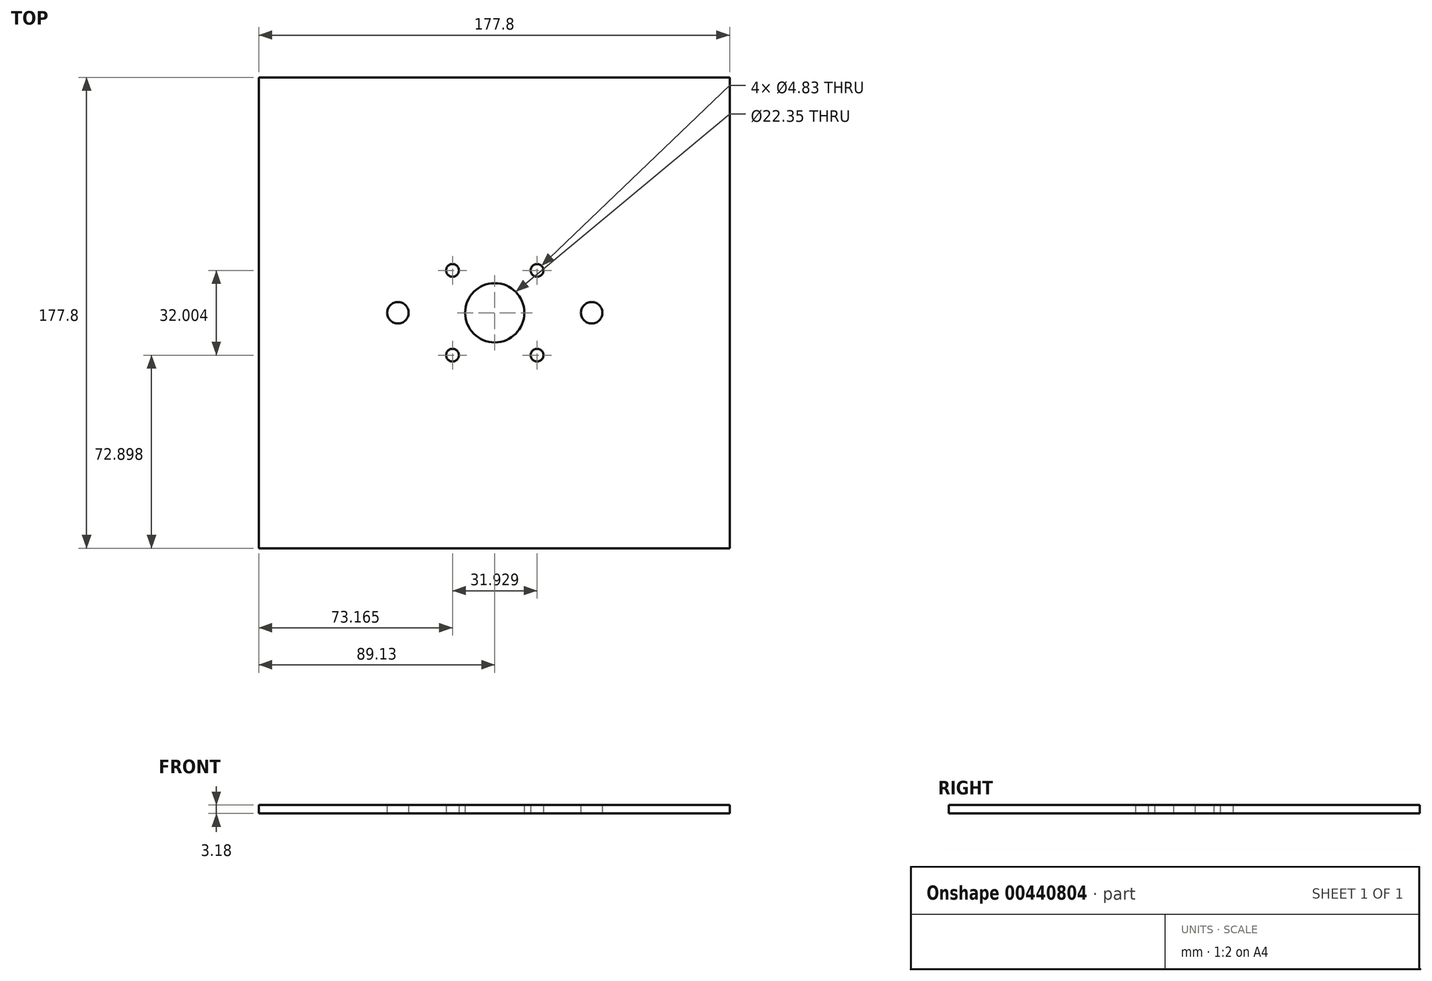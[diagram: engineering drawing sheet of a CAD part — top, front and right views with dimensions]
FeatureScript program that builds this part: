
annotation { "Feature Type Name" : "Feature", "Feature Type Description" : "" }
export const myFeature = defineFeature(function(context is Context, id is Id, definition is map)
    precondition{}
    {
        {
            var Q0;
            Q0=qCreatedBy(makeId("Top.planeOp"),FACE);
            var sketch = newSketch(context, id + "F0", { "sketchPlane" : qUnion([Q0])});
            skCircle(sketch, "E0", {"center": v(0.23, 0) * mm, "radius": 11.18 * mm});
            skCircle(sketch, "E1", {"center": v(16.2, 16) * mm, "radius": 2.41 * mm});
            skCircle(sketch, "E2.MirrorC", {"center": v(-15.74, 16) * mm, "radius": 2.41 * mm});
            skCircle(sketch, "E3.MirrorC", {"center": v(16.2, -16) * mm, "radius": 2.41 * mm});
            skCircle(sketch, "E4.MirrorC", {"center": v(-15.74, -16) * mm, "radius": 2.41 * mm});
            skPoint(sketch, "E5.startSnap0", {"position": v(8.57, 0) * mm});
            skPoint(sketch, "E5.endSnap0", {"position": v(8.57, 0) * mm});
            skCircle(sketch, "E6", {"center": v(-36.35, 0) * mm, "radius": 4.05 * mm});
            skCircle(sketch, "E7", {"center": v(36.8, 0) * mm, "radius": 4.05 * mm});
            skLineSegment(sketch, "E8.bottom", {"start": v(88.9, 88.9) * mm, "end": v(-88.9, 88.9) * mm});
            skLineSegment(sketch, "E8.top", {"start": v(88.9, -88.9) * mm, "end": v(-88.9, -88.9) * mm});
            skLineSegment(sketch, "E8.left", {"start": v(88.9, 88.9) * mm, "end": v(88.9, -88.9) * mm});
            skLineSegment(sketch, "E8.right", {"start": v(-88.9, 88.9) * mm, "end": v(-88.9, -88.9) * mm});
            skPoint(sketch, "E8.middle", {"position": v(0, 0) * mm});
            skSolve(sketch);
        }
        {
            var Q0;
            Q0 = qSketchRegion(id + "F0", true);
            extrude(context, id + "F1", {"entities" : qUnion([Q0]), "depth" : 3.17 * mm});
        }
    });
